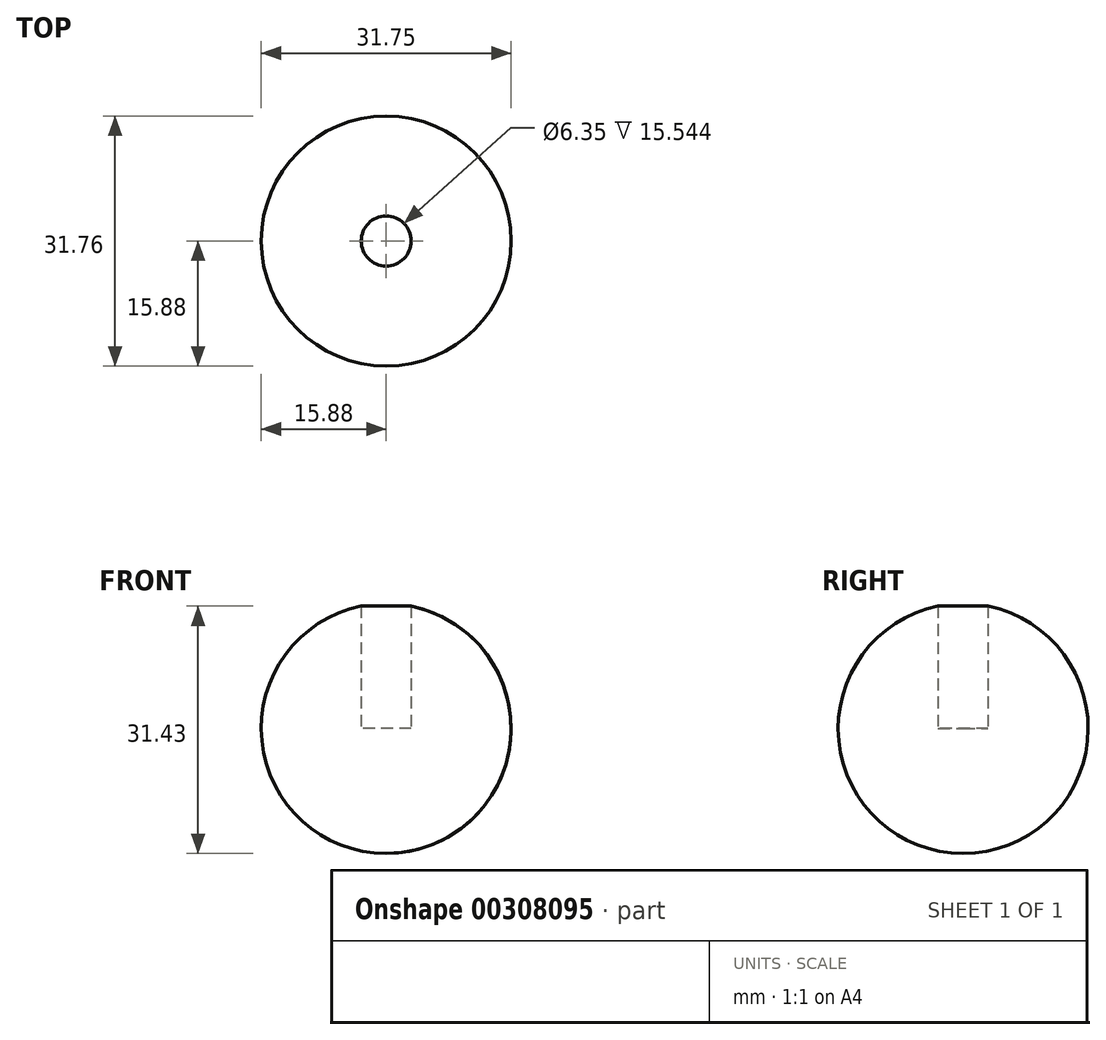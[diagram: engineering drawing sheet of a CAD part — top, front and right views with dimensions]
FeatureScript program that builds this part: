
annotation { "Feature Type Name" : "Feature", "Feature Type Description" : "" }
export const myFeature = defineFeature(function(context is Context, id is Id, definition is map)
    precondition{}
    {
        {
            var Q0;
            Q0=qCreatedBy(makeId("Front.planeOp"),FACE);
            var sketch = newSketch(context, id + "F0", { "sketchPlane" : qUnion([Q0])});
            skArc(sketch, "E0", {"start": v(0, 15.88) * mm, "mid": v(-15.88, 0) * mm, "end": v(0, -15.88) * mm});
            skLineSegment(sketch, "E1", {"start": v(0, 15.88) * mm, "end": v(0, -15.88) * mm});
            skSolve(sketch);
        }
        {
            var Q0;
            Q0=qCreatedBy(makeId("Top.planeOp"),FACE);
            var sketch = newSketch(context, id + "F1", { "sketchPlane" : qUnion([Q0])});
            skCircle(sketch, "E2", {"center": v(0, 0) * mm, "radius": 15.88 * mm});
            skSolve(sketch);
        }
        {
            var Q0;
            Q0=makeQuery(id+"F0.imprint","IMPRINT",FACE,{"disambiguationData":[TD([[makeQuery(id+"F0.imprint","IMPRINT",EDGE,{"derivedFrom":sQuery(id+"F0.wireOp",EDGE,"E0")}),1.0]])]});
            var Q1;
            Q1=sQuery(id+"F1.wireOp",EDGE,"E2");
            revolve(context, id + "F2", {"entities" : qUnion([Q0]), "axis" : qUnion([Q1]), "revolveType" : RevolveType.FULL});
        }
        {
            var Q0;
            Q0=qCreatedBy(makeId("Top.planeOp"),FACE);
            cPlane(context, id + "F3", {"entities" : qUnion([Q0]), "cplaneType" : CPlaneType.OFFSET, "offset" : 2 / 203.2 * mm, "width" : 152.4 * mm, "height" : 152.4 * mm});
        }
        {
            var Q0;
            Q0=qCreatedBy(id+"F3.planeOp",FACE);
            var sketch = newSketch(context, id + "F4", { "sketchPlane" : qUnion([Q0])});
            skCircle(sketch, "E3", {"center": v(0, 0) * mm, "radius": 3.18 * mm});
            skSolve(sketch);
        }
        {
            var Q0;
            Q0=qSketchRegion(id+"F4",true);
            extrude(context, id + "F5", {"entities" : qUnion([Q0]), "depth" : 50.8 * mm});
        }
        {
            var Q0;
            Q0=makeQuery(id+"F5.opExtrude","SWEPT_BODY",BODY,{"disambiguationData":[OSD([sQuery(id+"F4.wireOp",EDGE,"E3")])]});
            var Q1;
            Q1=makeQuery(id+"F5LJcq3Kl6RkE3x_2.opPattern","COPY",BODY,{"derivedFrom":makeQuery(id+"F5.opExtrude","SWEPT_BODY",BODY,{"disambiguationData":[OSD([sQuery(id+"F4.wireOp",EDGE,"E3")])]}),"instanceName":"1"});
            var Q2;
            Q2=makeQuery(id+"FregfX3WhNtuXeo_2.opPattern","COPY",BODY,{"derivedFrom":makeQuery(id+"F5.opExtrude","SWEPT_BODY",BODY,{"disambiguationData":[OSD([sQuery(id+"F4.wireOp",EDGE,"E3")])]}),"instanceName":"1"});
            var Q3;
            Q3=makeQuery(id+"F2.opRevolve","SWEPT_BODY",BODY,{"disambiguationData":[OSD([sQuery(id+"F0.wireOp",EDGE,"E0"),sQuery(id+"F0.wireOp",EDGE,"E1")])]});
            booleanBodies(context, id + "F6", {"operationType" : BooleanOperationType.SUBTRACTION, "tools" : qUnion([Q0, Q1, Q2]), "targets" : qUnion([Q3])});
        }
    });
